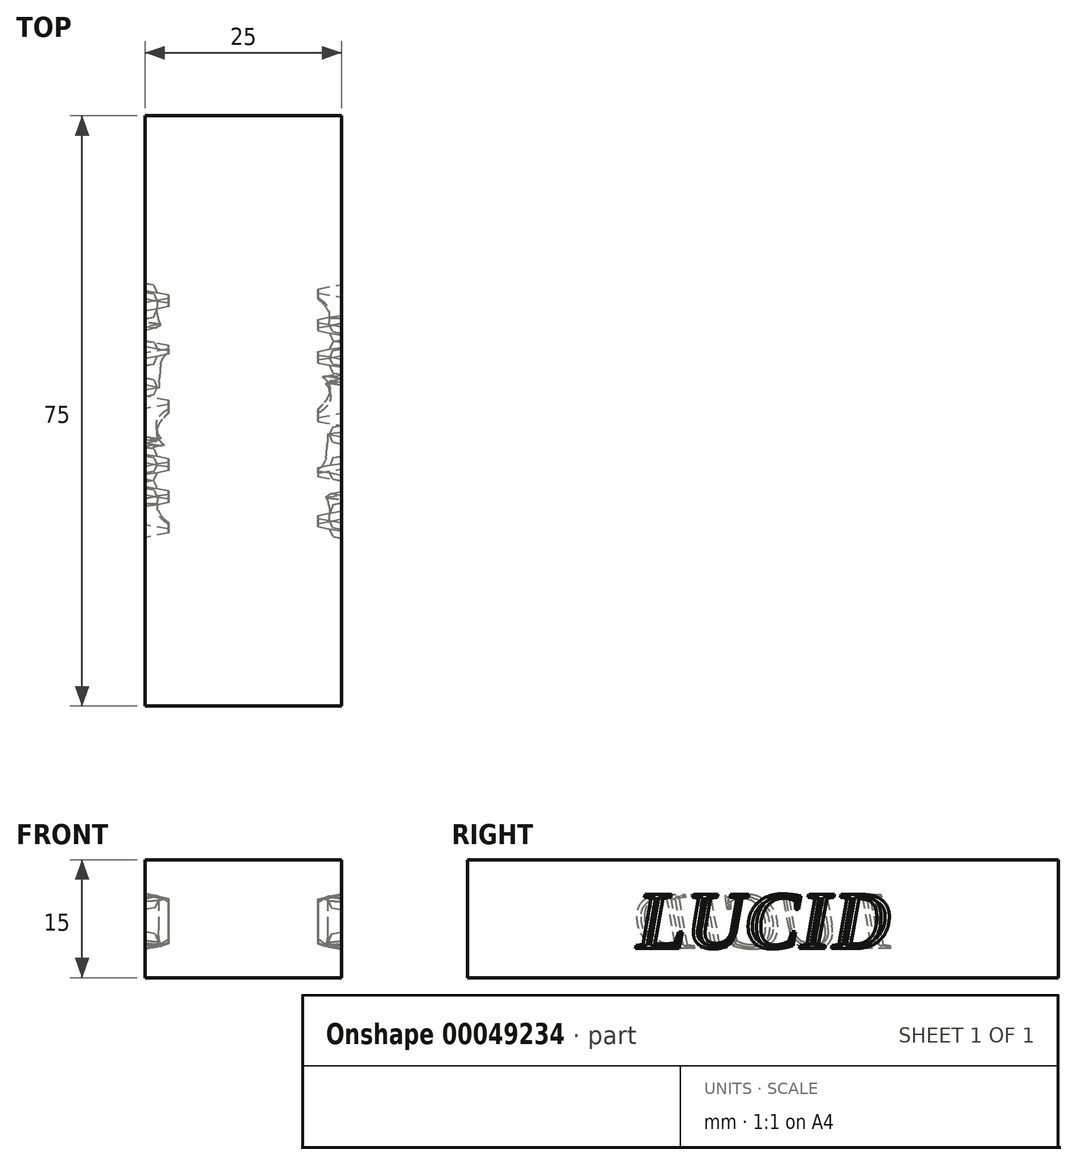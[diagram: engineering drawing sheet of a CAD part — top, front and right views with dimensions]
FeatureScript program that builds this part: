
annotation { "Feature Type Name" : "Feature", "Feature Type Description" : "" }
export const myFeature = defineFeature(function(context is Context, id is Id, definition is map)
    precondition{}
    {
        {
            var Q0;
            Q0=qCreatedBy(makeId("Front.planeOp"),FACE);
            var sketch = newSketch(context, id + "F0", { "sketchPlane" : qUnion([Q0])});
            skLineSegment(sketch, "E0", {"start": v(-12.5, 15.21) * mm, "end": v(0, 15.21) * mm});
            skLineSegment(sketch, "E1", {"start": v(0, 15.21) * mm, "end": v(0, 0.21) * mm});
            skLineSegment(sketch, "E2", {"start": v(0, 0.21) * mm, "end": v(-12.5, 0.21) * mm});
            skLineSegment(sketch, "E3", {"start": v(-12.5, 0.21) * mm, "end": v(-12.5, 15.21) * mm});
            skSolve(sketch);
        }
        {
            var Q0;
            Q0=makeQuery(id+"F0.imprint","IMPRINT",FACE,{"disambiguationData":[TD([[makeQuery(id+"F0.imprint","IMPRINT",EDGE,{"derivedFrom":sQuery(id+"F0.wireOp",EDGE,"E0")}),-1.0]])]});
            extrude(context, id + "F1", {"entities" : qUnion([Q0]), "depth" : 75 * mm});
        }
        {
            var Q0;
            Q0=makeQuery(id+"F1.opExtrude","SWEPT_FACE",FACE,{"disambiguationData":[OSD([sQuery(id+"F0.wireOp",EDGE,"E3")])]});
            var sketch = newSketch(context, id + "F2", { "sketchPlane" : qUnion([Q0])});
            skText(sketch, "E4", { "text": "LUCID", "fontName": "Tinos-BoldItalic.ttf"});
            const initialGuessF2  = {"E4": [0.02138, 0.00396, 1, 0, 0.0075]};
            skSetInitialGuess(sketch, initialGuessF2);
            skSolve(sketch);
        }
        {
            var Q0;
            Q0=makeQuery(id+"F2.imprint","IMPRINT",FACE,{"disambiguationData":[TD([[makeQuery(id+"F2.imprint","IMPRINT",EDGE,{"derivedFrom":sQuery(id+"F2.wireOp",EDGE,"E4.sketch_text.stroke-39")}),-1.0]])]});
            var Q1;
            Q1=makeQuery(id+"F2.imprint","IMPRINT",FACE,{"disambiguationData":[TD([[makeQuery(id+"F2.imprint","IMPRINT",EDGE,{"derivedFrom":sQuery(id+"F2.wireOp",EDGE,"E4.sketch_text.stroke-62")}),-1.0]])]});
            var Q2;
            Q2=makeQuery(id+"F2.imprint","IMPRINT",FACE,{"disambiguationData":[TD([[makeQuery(id+"F2.imprint","IMPRINT",EDGE,{"derivedFrom":sQuery(id+"F2.wireOp",EDGE,"E4.sketch_text.stroke-74")}),-1.0]])]});
            var Q3;
            Q3=makeQuery(id+"F2.imprint","IMPRINT",FACE,{"disambiguationData":[TD([[makeQuery(id+"F2.imprint","IMPRINT",EDGE,{"derivedFrom":sQuery(id+"F2.wireOp",EDGE,"E4.sketch_text.stroke-16")}),-1.0]])]});
            var Q4;
            Q4=makeQuery(id+"F2.imprint","IMPRINT",FACE,{"disambiguationData":[TD([[makeQuery(id+"F2.imprint","IMPRINT",EDGE,{"derivedFrom":sQuery(id+"F2.wireOp",EDGE,"E4.sketch_text.stroke-0")}),-1.0]])]});
            extrude(context, id + "F3", {"entities" : qUnion([Q0, Q1, Q2, Q3, Q4]), "operationType" : NewBodyOperationType.REMOVE, "oppositeDirection" : true, "depth" : 3 * mm, "hasDraft" : true, "draftAngle" : 10 * degree, "draftPullDirection" : true});
        }
        {
            var Q0;
            Q0=qCreatedBy(makeId("Right.planeOp"),FACE);
            var sketch = newSketch(context, id + "F4", { "sketchPlane" : qUnion([Q0])});
            skLineSegment(sketch, "E5", {"start": v(-37.5, 26.3) * mm, "end": v(-37.5, -10.84) * mm});
            skSolve(sketch);
        }
        {
            var Q0;
            Q0=makeQuery(id+"F1.opExtrude","SWEPT_BODY",BODY,{"disambiguationData":[OSD([sQuery(id+"F0.wireOp",EDGE,"E0"),sQuery(id+"F0.wireOp",EDGE,"E1"),sQuery(id+"F0.wireOp",EDGE,"E2"),sQuery(id+"F0.wireOp",EDGE,"E3")])]});
            var Q1;
            Q1=sQuery(id+"F4.wireOp",EDGE,"E5");
            circularPattern(context, id + "F5", {"operationType" : NewBodyOperationType.ADD, "entities" : qUnion([Q0]), "axis" : qUnion([Q1]), "angle" : 180 * degree, "instanceCount" : 2, "equalSpace" : true});
        }
    });
